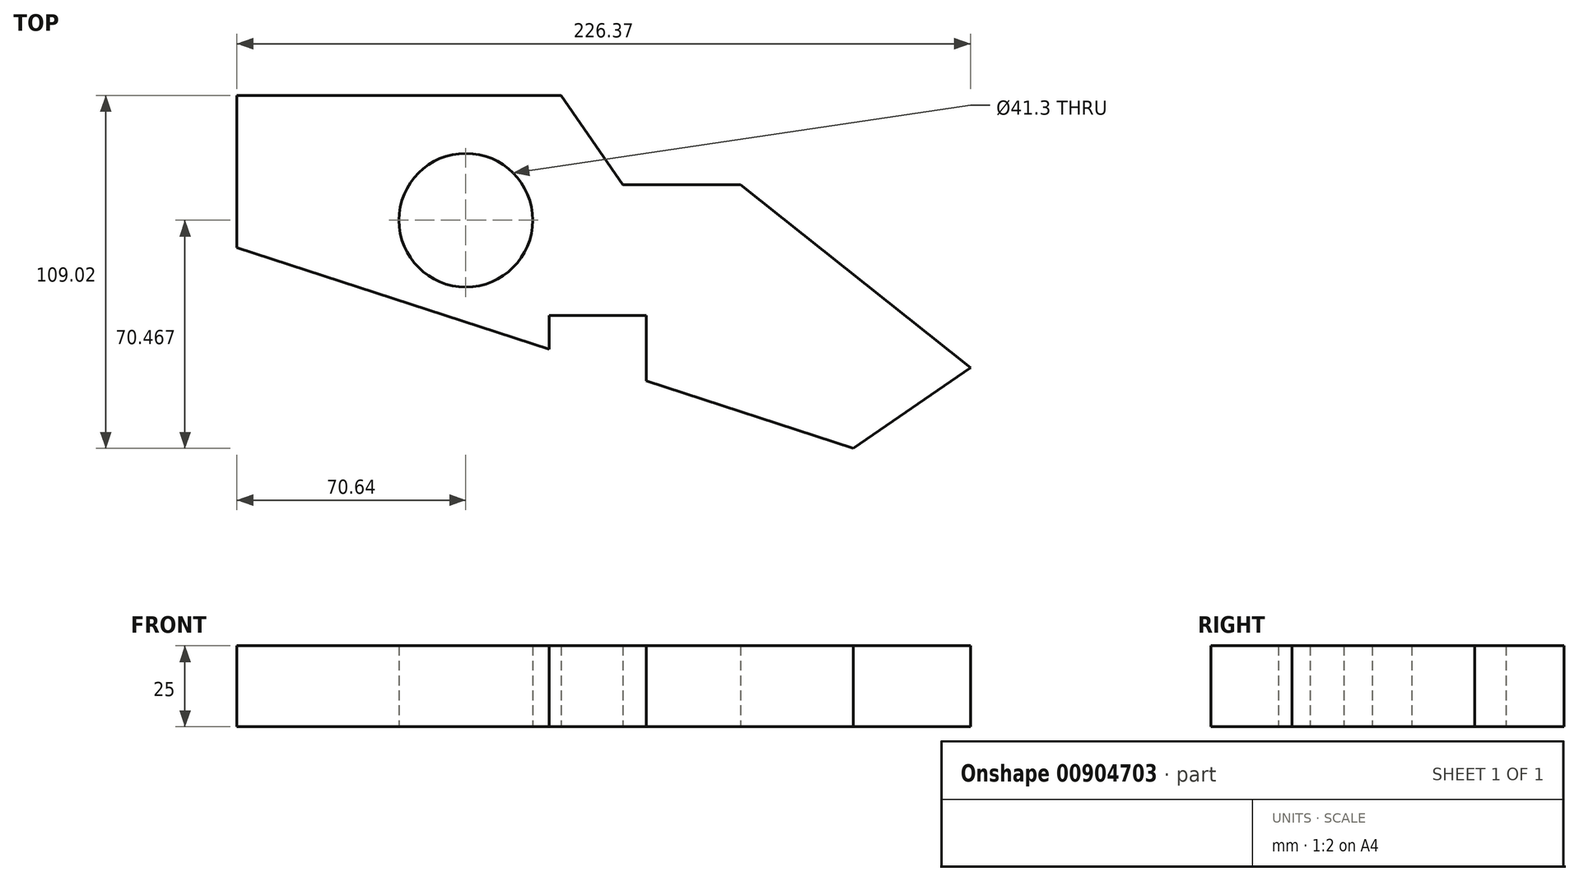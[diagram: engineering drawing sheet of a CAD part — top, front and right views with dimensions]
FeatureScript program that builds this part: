
annotation { "Feature Type Name" : "Feature", "Feature Type Description" : "" }
export const myFeature = defineFeature(function(context is Context, id is Id, definition is map)
    precondition{}
    {
        {
            var Q0;
            Q0=qCreatedBy(makeId("Top.planeOp"),FACE);
            var sketch = newSketch(context, id + "F0", { "sketchPlane" : qUnion([Q0])});
            skLineSegment(sketch, "E0", {"start": v(-70.64, 67.97) * mm, "end": v(29.36, 67.97) * mm});
            skLineSegment(sketch, "E1", {"start": v(29.36, 67.97) * mm, "end": v(48.4, 40.36) * mm});
            skLineSegment(sketch, "E2", {"start": v(48.4, 40.36) * mm, "end": v(84.71, 40.36) * mm});
            skLineSegment(sketch, "E3", {"start": v(84.71, 40.36) * mm, "end": v(155.73, -16.08) * mm});
            skLineSegment(sketch, "E4", {"start": v(155.73, -16.08) * mm, "end": v(119.5, -41.05) * mm});
            skLineSegment(sketch, "E5", {"start": v(119.5, -41.05) * mm, "end": v(-70.64, 20.94) * mm});
            skLineSegment(sketch, "E6", {"start": v(-70.64, 20.94) * mm, "end": v(-70.64, 67.97) * mm});
            skLineSegment(sketch, "E7", {"start": v(-191.1, -57.22) * mm, "end": v(-179.46, 33.99) * mm});
            skLineSegment(sketch, "E8", {"start": v(-179.46, 33.99) * mm, "end": v(-122, 34.72) * mm});
            skLineSegment(sketch, "E9", {"start": v(-122, 34.72) * mm, "end": v(-120.84, -57.22) * mm});
            skLineSegment(sketch, "E10", {"start": v(-120.84, -57.22) * mm, "end": v(-191.1, -57.22) * mm});
            skLineSegment(sketch, "E11", {"start": v(-179.46, 33.99) * mm, "end": v(-120.84, -57.22) * mm});
            skCircle(sketch, "E12", {"center": v(0, 29.42) * mm, "radius": 20.65 * mm});
            skSolve(sketch);
        }
        {
            var Q0;
            Q0=makeQuery(id+"F0.imprint","IMPRINT",FACE,{"disambiguationData":[TD([[makeQuery(id+"F0.imprint","IMPRINT",EDGE,{"derivedFrom":sQuery(id+"F0.wireOp",EDGE,"E0")}),-1.0]])]});
            extrude(context, id + "F1", {"entities" : qUnion([Q0]), "depth" : 25 * mm, "offsetDistance" : 25 * mm});
        }
        {
            var Q0;
            Q0=qCreatedBy(makeId("Top.planeOp"),FACE);
            var sketch = newSketch(context, id + "F2", { "sketchPlane" : qUnion([Q0])});
            skLineSegment(sketch, "E13.bottom", {"start": v(55.67, -32.01) * mm, "end": v(25.67, -32.01) * mm});
            skLineSegment(sketch, "E13.top", {"start": v(55.67, 0) * mm, "end": v(25.67, 0) * mm});
            skLineSegment(sketch, "E13.left", {"start": v(55.67, -32.01) * mm, "end": v(55.67, 0) * mm});
            skLineSegment(sketch, "E13.right", {"start": v(25.67, -32.01) * mm, "end": v(25.67, 0) * mm});
            skSolve(sketch);
        }
        {
            var Q0;
            Q0=makeQuery(id+"F2.imprint","IMPRINT",FACE,{"disambiguationData":[TD([[makeQuery(id+"F2.imprint","IMPRINT",EDGE,{"derivedFrom":sQuery(id+"F2.wireOp",EDGE,"E13.bottom")}),-1.0]])]});
            extrude(context, id + "F3", {"entities" : qUnion([Q0]), "operationType" : NewBodyOperationType.REMOVE, "depth" : 25 * mm, "offsetDistance" : 25 * mm});
        }
    });
